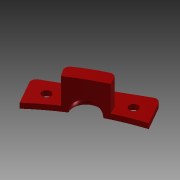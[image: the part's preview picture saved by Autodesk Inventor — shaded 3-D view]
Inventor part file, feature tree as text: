
AUTODESK INVENTOR PART (.ipt)
format: ipt  version: 2015 SP1 (Build 190203100, 203)  size: 154,112 bytes
history: native  units: mm
features: reference x5, sketch x3, extrude x2, plane x1, revolve x1, fillet x1
ambient origin geometry x8: Origin, YZ Plane, XZ Plane, XY Plane, X Axis, Y Axis, Z Axis, Center Point
bodies: Solid1 (feature_tree)
feature tree (13):
  plane  "Work Plane1"
  extrude  "Extrusion1"  Depth=12.0mm
  extrude  "Extrusion2"  Depth=2.0mm
  revolve  "Revolution1"  [1 undecoded]
  fillet  "Fillet1"  Radius=10.0mm
  sketch  "Sketch1"  dims[d0=12.0mm d1=12.0mm]
  reference  "Reference1"
  reference  "Reference2"
  reference  "Reference5"
  reference  "Reference6"
  reference  "Reference7"
  sketch  "Sketch2"  dims[d2=2.0mm d4=180.0mm]
  sketch  "Sketch3"  dims[d5=2.0mm d6=0.0mm d7=10.0mm d8=10.0mm d9=2.0mm d10=10.0mm d11=0.0mm d12=10.0mm d13=90.0deg d14=2.0mm]
note: 1 required parameter value undecoded (feature->parameter linkage not recoverable at this tier; creation-order binding heuristic only, values carry confidence <= 0.55)
